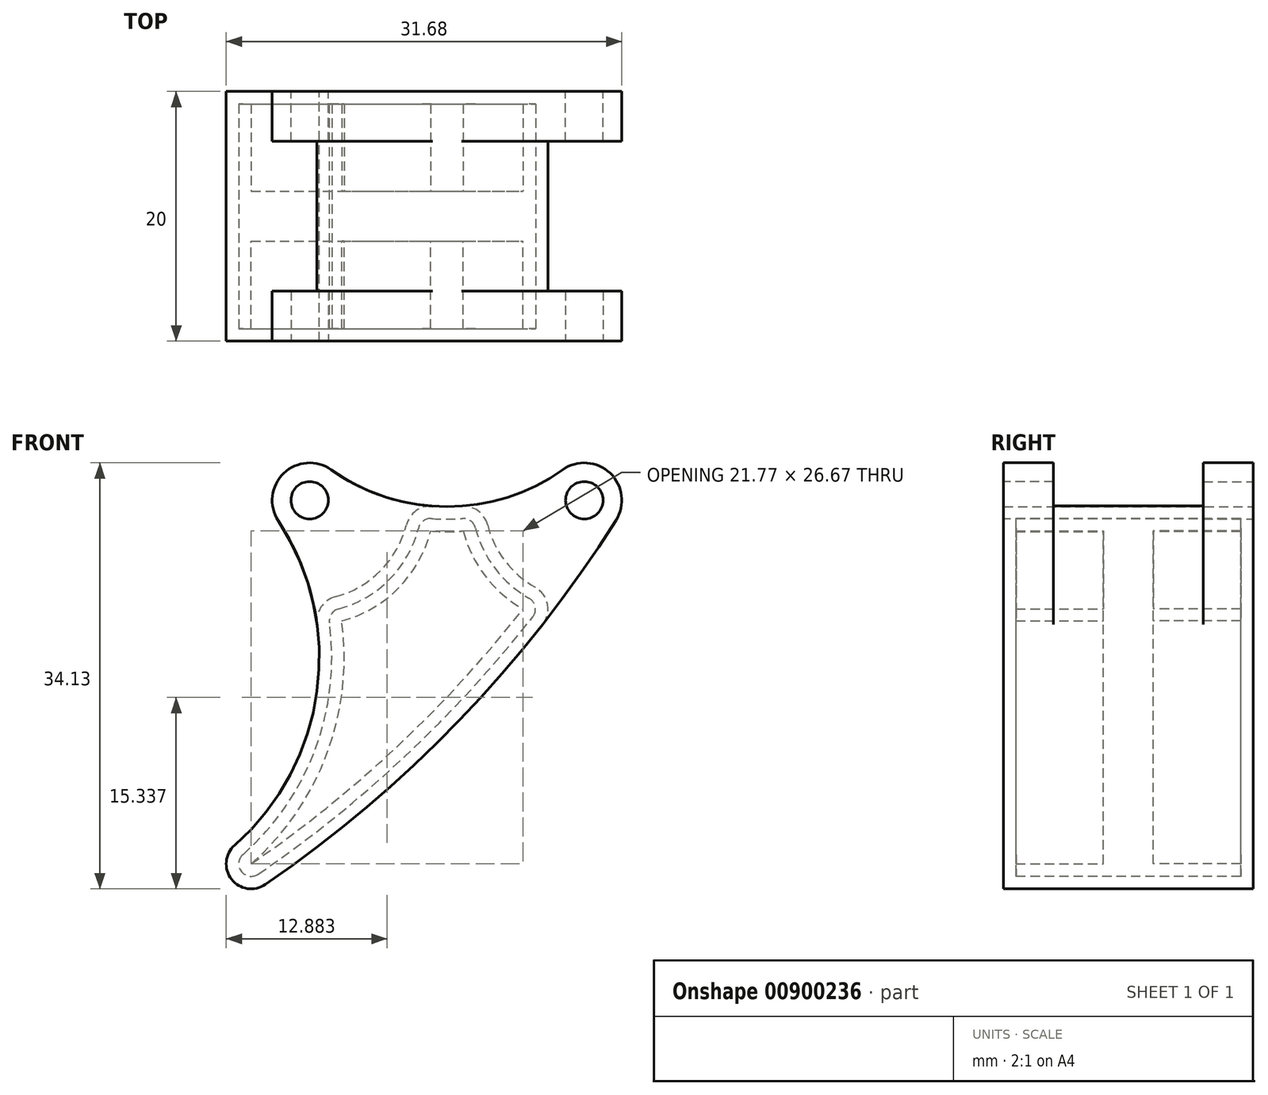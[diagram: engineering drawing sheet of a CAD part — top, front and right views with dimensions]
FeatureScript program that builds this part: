
annotation { "Feature Type Name" : "Feature", "Feature Type Description" : "" }
export const myFeature = defineFeature(function(context is Context, id is Id, definition is map)
    precondition{}
    {
        {
            var Q0;
            Q0=qCreatedBy(makeId("Front.planeOp"),FACE);
            var sketch = newSketch(context, id + "F0", { "sketchPlane" : qUnion([Q0])});
            skArc(sketch, "E0", {"start": v(1.74, 2.45) * mm, "mid": v(-2.08, 2.16) * mm, "end": v(-2.5, -1.65) * mm});
            skArc(sketch, "E1", {"start": v(24.54, -1.6) * mm, "mid": v(24.06, 2.18) * mm, "end": v(20.26, 2.45) * mm});
            skArc(sketch, "E2", {"start": v(1.74, 2.45) * mm, "mid": v(11, -0.5) * mm, "end": v(20.26, 2.45) * mm});
            skArc(sketch, "E3", {"start": v(-6, -27.63) * mm, "mid": v(0.6, -15.29) * mm, "end": v(-2.5, -1.65) * mm});
            skArc(sketch, "E4", {"start": v(-6, -27.63) * mm, "mid": v(-6.26, -30.35) * mm, "end": v(-3.55, -30.78) * mm});
            skArc(sketch, "E5", {"start": v(-3.55, -30.78) * mm, "mid": v(11.99, -17.62) * mm, "end": v(24.54, -1.6) * mm});
            skSolve(sketch);
        }
        {
            var Q0;
            Q0=makeQuery(id+"F0.imprint","IMPRINT",FACE,{"disambiguationData":[TD([[makeQuery(id+"F0.imprint","IMPRINT",EDGE,{"derivedFrom":sQuery(id+"F0.wireOp",EDGE,"E0")}),1.0]])]});
            extrude(context, id + "F1", {"entities" : qUnion([Q0]), "depth" : 4 * mm, "offsetDistance" : 25 * mm});
        }
        {
            var Q0;
            Q0=makeQuery(id+"F1.opExtrude","CAP_FACE",FACE,{"disambiguationData":[OSD([sQuery(id+"F0.wireOp",EDGE,"E0"),sQuery(id+"F0.wireOp",EDGE,"E1"),sQuery(id+"F0.wireOp",EDGE,"E2"),sQuery(id+"F0.wireOp",EDGE,"E3"),sQuery(id+"F0.wireOp",EDGE,"E4"),sQuery(id+"F0.wireOp",EDGE,"E5")])],"isStart":false});
            var sketch = newSketch(context, id + "F2", { "sketchPlane" : qUnion([Q0])});
            skArc(sketch, "E6", {"start": v(2.06, -7.73) * mm, "mid": v(5.69, -5.62) * mm, "end": v(7.75, -1.97) * mm});
            skArc(sketch, "E7", {"start": v(14.25, -1.97) * mm, "mid": v(15.65, -4.86) * mm, "end": v(18.07, -6.97) * mm});
            skArc(sketch, "E8.0", {"start": v(9.84, -0.47) * mm, "mid": v(11, -0.5) * mm, "end": v(12.16, -0.47) * mm});
            skArc(sketch, "E9.0", {"start": v(-6, -27.63) * mm, "mid": v(-0.49, -19.6) * mm, "end": v(0.6, -9.93) * mm});
            skArc(sketch, "E10.0", {"start": v(-6, -27.63) * mm, "mid": v(-6.26, -30.35) * mm, "end": v(-3.55, -30.78) * mm});
            skArc(sketch, "E11.0", {"start": v(-3.55, -30.78) * mm, "mid": v(8.35, -21.21) * mm, "end": v(18.66, -9.94) * mm});
            skPoint(sketch, "E12.newPointB", {"position": v(-2.5, -1.65) * mm});
            skArc(sketch, "E12.filletArc", {"start": v(2.06, -7.73) * mm, "mid": v(0.9, -8.55) * mm, "end": v(0.6, -9.93) * mm});
            skPoint(sketch, "E13.newPointB", {"position": v(1.74, 2.45) * mm});
            skArc(sketch, "E13.filletArc", {"start": v(9.84, -0.47) * mm, "mid": v(8.52, -0.84) * mm, "end": v(7.75, -1.97) * mm});
            skPoint(sketch, "E14.newPointA", {"position": v(20.26, 2.45) * mm});
            skArc(sketch, "E14.filletArc", {"start": v(14.25, -1.97) * mm, "mid": v(13.48, -0.84) * mm, "end": v(12.16, -0.47) * mm});
            skPoint(sketch, "E15.newPointB", {"position": v(24.54, -1.6) * mm});
            skArc(sketch, "E15.filletArc", {"start": v(18.66, -9.94) * mm, "mid": v(19.05, -8.32) * mm, "end": v(18.07, -6.97) * mm});
            skSolve(sketch);
        }
        {
            var Q0;
            Q0=makeQuery(id+"F2.imprint","IMPRINT",FACE,{"disambiguationData":[TD([[makeQuery(id+"F2.imprint","IMPRINT",EDGE,{"derivedFrom":sQuery(id+"F2.wireOp",EDGE,"E6")}),-1.0]])]});
            extrude(context, id + "F3", {"entities" : qUnion([Q0]), "operationType" : NewBodyOperationType.ADD, "depth" : 6 * mm, "offsetDistance" : 25 * mm});
        }
        {
            var Q0;
            Q0=makeQuery(id+"F3.opExtrude","CAP_FACE",FACE,{"disambiguationData":[OSD([sQuery(id+"F2.wireOp",EDGE,"E6"),sQuery(id+"F2.wireOp",EDGE,"E7"),sQuery(id+"F2.wireOp",EDGE,"E8.0"),sQuery(id+"F2.wireOp",EDGE,"E9.0"),sQuery(id+"F2.wireOp",EDGE,"E10.0"),sQuery(id+"F2.wireOp",EDGE,"E11.0"),sQuery(id+"F2.wireOp",EDGE,"E12.filletArc"),sQuery(id+"F2.wireOp",EDGE,"E13.filletArc"),sQuery(id+"F2.wireOp",EDGE,"E14.filletArc"),sQuery(id+"F2.wireOp",EDGE,"E15.filletArc")])],"isStart":false});
            var sketch = newSketch(context, id + "F4", { "sketchPlane" : qUnion([Q0])});
            skArc(sketch, "E16.0.0", {"start": v(-3.55, -30.78) * mm, "mid": v(8.35, -21.21) * mm, "end": v(18.66, -9.94) * mm});
            skArc(sketch, "E16.0.1", {"start": v(18.66, -9.94) * mm, "mid": v(19.05, -8.32) * mm, "end": v(18.07, -6.97) * mm});
            skArc(sketch, "E16.0.2", {"start": v(18.07, -6.97) * mm, "mid": v(15.65, -4.86) * mm, "end": v(14.25, -1.97) * mm});
            skArc(sketch, "E16.0.3", {"start": v(14.25, -1.97) * mm, "mid": v(13.48, -0.84) * mm, "end": v(12.16, -0.47) * mm});
            skArc(sketch, "E16.0.4", {"start": v(12.16, -0.47) * mm, "mid": v(11, -0.5) * mm, "end": v(9.84, -0.47) * mm});
            skArc(sketch, "E16.0.5", {"start": v(9.84, -0.47) * mm, "mid": v(8.52, -0.84) * mm, "end": v(7.75, -1.97) * mm});
            skArc(sketch, "E16.0.6", {"start": v(7.75, -1.97) * mm, "mid": v(5.69, -5.62) * mm, "end": v(2.06, -7.73) * mm});
            skArc(sketch, "E16.0.7", {"start": v(2.06, -7.73) * mm, "mid": v(0.9, -8.55) * mm, "end": v(0.6, -9.93) * mm});
            skArc(sketch, "E16.0.8", {"start": v(0.6, -9.93) * mm, "mid": v(-0.49, -19.6) * mm, "end": v(-6, -27.63) * mm});
            skArc(sketch, "E16.0.9", {"start": v(-6, -27.63) * mm, "mid": v(-6.26, -30.35) * mm, "end": v(-3.55, -30.78) * mm});
            skArc(sketch, "E17.0", {"start": v(-5.34, -28.38) * mm, "mid": v(-5.47, -29.74) * mm, "end": v(-4.12, -29.95) * mm});
            skArc(sketch, "E17.1", {"start": v(1.58, -9.8) * mm, "mid": v(0.45, -19.96) * mm, "end": v(-5.34, -28.38) * mm});
            skArc(sketch, "E17.2", {"start": v(-4.12, -29.95) * mm, "mid": v(7.67, -20.48) * mm, "end": v(17.87, -9.33) * mm});
            skArc(sketch, "E17.3", {"start": v(2.32, -8.7) * mm, "mid": v(1.74, -9.1) * mm, "end": v(1.58, -9.8) * mm});
            skArc(sketch, "E17.4", {"start": v(8.72, -2.21) * mm, "mid": v(6.4, -6.33) * mm, "end": v(2.32, -8.7) * mm});
            skArc(sketch, "E17.5", {"start": v(9.77, -1.46) * mm, "mid": v(9.1, -1.65) * mm, "end": v(8.72, -2.21) * mm});
            skArc(sketch, "E17.6", {"start": v(17.87, -9.33) * mm, "mid": v(18.07, -8.52) * mm, "end": v(17.58, -7.84) * mm});
            skArc(sketch, "E17.7", {"start": v(17.58, -7.84) * mm, "mid": v(14.85, -5.47) * mm, "end": v(13.28, -2.21) * mm});
            skArc(sketch, "E17.8", {"start": v(13.28, -2.21) * mm, "mid": v(12.9, -1.65) * mm, "end": v(12.23, -1.46) * mm});
            skArc(sketch, "E17.9", {"start": v(12.23, -1.46) * mm, "mid": v(11, -1.5) * mm, "end": v(9.77, -1.46) * mm});
            skSolve(sketch);
        }
        {
            var Q0;
            Q0=makeQuery(id+"F4.imprint","IMPRINT",FACE,{"disambiguationData":[TD([[makeQuery(id+"F4.imprint","IMPRINT",EDGE,{"derivedFrom":sQuery(id+"F4.wireOp",EDGE,"E17.0")}),1.0]])]});
            extrude(context, id + "F5", {"entities" : qUnion([Q0]), "operationType" : NewBodyOperationType.REMOVE, "oppositeDirection" : true, "depth" : 2 * mm, "offsetDistance" : 25 * mm});
        }
        {
            var Q0;
            Q0=makeQuery(id+"F5.boolean.opBoolean","COPY",FACE,{"derivedFrom":makeQuery(id+"F5.opExtrude","CAP_FACE",FACE,{"disambiguationData":[OSD([sQuery(id+"F4.wireOp",EDGE,"E17.0"),sQuery(id+"F4.wireOp",EDGE,"E17.1"),sQuery(id+"F4.wireOp",EDGE,"E17.2"),sQuery(id+"F4.wireOp",EDGE,"E17.3"),sQuery(id+"F4.wireOp",EDGE,"E17.4"),sQuery(id+"F4.wireOp",EDGE,"E17.5"),sQuery(id+"F4.wireOp",EDGE,"E17.6"),sQuery(id+"F4.wireOp",EDGE,"E17.7"),sQuery(id+"F4.wireOp",EDGE,"E17.8"),sQuery(id+"F4.wireOp",EDGE,"E17.9")])],"isStart":false})});
            var sketch = newSketch(context, id + "F6", { "sketchPlane" : qUnion([Q0])});
            skArc(sketch, "E18.0.0", {"start": v(13.28, -2.21) * mm, "mid": v(12.9, -1.65) * mm, "end": v(12.23, -1.46) * mm});
            skArc(sketch, "E18.0.1", {"start": v(12.23, -1.46) * mm, "mid": v(11, -1.5) * mm, "end": v(9.77, -1.46) * mm});
            skArc(sketch, "E18.0.2", {"start": v(9.77, -1.46) * mm, "mid": v(9.1, -1.65) * mm, "end": v(8.72, -2.21) * mm});
            skArc(sketch, "E18.0.3", {"start": v(8.72, -2.21) * mm, "mid": v(6.4, -6.33) * mm, "end": v(2.32, -8.7) * mm});
            skArc(sketch, "E18.0.4", {"start": v(2.32, -8.7) * mm, "mid": v(1.74, -9.1) * mm, "end": v(1.58, -9.8) * mm});
            skArc(sketch, "E18.0.5", {"start": v(1.58, -9.8) * mm, "mid": v(0.45, -19.96) * mm, "end": v(-5.34, -28.38) * mm});
            skArc(sketch, "E18.0.6", {"start": v(-5.34, -28.38) * mm, "mid": v(-5.47, -29.74) * mm, "end": v(-4.12, -29.95) * mm});
            skArc(sketch, "E18.0.7", {"start": v(-4.12, -29.95) * mm, "mid": v(7.67, -20.48) * mm, "end": v(17.87, -9.33) * mm});
            skArc(sketch, "E18.0.8", {"start": v(17.87, -9.33) * mm, "mid": v(18.07, -8.52) * mm, "end": v(17.58, -7.84) * mm});
            skArc(sketch, "E18.0.9", {"start": v(17.58, -7.84) * mm, "mid": v(14.85, -5.47) * mm, "end": v(13.28, -2.21) * mm});
            skArc(sketch, "E19.0", {"start": v(17.09, -8.71) * mm, "mid": v(14.06, -6.08) * mm, "end": v(12.3, -2.46) * mm});
            skLineSegment(sketch, "E19.1", {"start": v(17.09, -8.71) * mm, "end": v(17.09, -8.71) * mm});
            skLineSegment(sketch, "E19.2", {"start": v(12.3, -2.46) * mm, "end": v(12.3, -2.46) * mm});
            skArc(sketch, "E19.3", {"start": v(-4.68, -29.13) * mm, "mid": v(6.98, -19.75) * mm, "end": v(17.09, -8.71) * mm});
            skLineSegment(sketch, "E19.4", {"start": v(-4.68, -29.13) * mm, "end": v(-4.68, -29.13) * mm});
            skArc(sketch, "E19.5", {"start": v(2.57, -9.66) * mm, "mid": v(1.39, -20.3) * mm, "end": v(-4.68, -29.13) * mm});
            skArc(sketch, "E19.6", {"start": v(12.3, -2.46) * mm, "mid": v(11, -2.5) * mm, "end": v(9.7, -2.46) * mm});
            skLineSegment(sketch, "E19.7", {"start": v(9.7, -2.46) * mm, "end": v(9.7, -2.46) * mm});
            skArc(sketch, "E19.8", {"start": v(9.7, -2.46) * mm, "mid": v(7.11, -7.03) * mm, "end": v(2.57, -9.66) * mm});
            skLineSegment(sketch, "E19.9", {"start": v(2.57, -9.66) * mm, "end": v(2.57, -9.66) * mm});
            skSolve(sketch);
        }
        {
            var Q0;
            Q0=makeQuery(id+"F6.imprint","IMPRINT",FACE,{"disambiguationData":[TD([[makeQuery(id+"F6.imprint","IMPRINT",EDGE,{"derivedFrom":sQuery(id+"F6.wireOp",EDGE,"E19.0")}),1.0]])]});
            extrude(context, id + "F7", {"entities" : qUnion([Q0]), "operationType" : NewBodyOperationType.REMOVE, "oppositeDirection" : true, "depth" : 7 * mm, "offsetDistance" : 25 * mm});
        }
        {
            var Q0;
            Q0=qCreatedBy(makeId("Front.planeOp"),FACE);
            var sketch = newSketch(context, id + "F8", { "sketchPlane" : qUnion([Q0])});
            skCircle(sketch, "E20", {"center": v(0, 0) * mm, "radius": 1.5 * mm});
            skCircle(sketch, "E21", {"center": v(22, 0) * mm, "radius": 1.5 * mm});
            skSolve(sketch);
        }
        {
            var Q0;
            Q0 = qSketchRegion(id + "F8", true);
            extrude(context, id + "F9", {"entities" : qUnion([Q0]), "operationType" : NewBodyOperationType.REMOVE, "endBound" : BoundingType.THROUGH_ALL, "depth" : 25 * mm, "offsetDistance" : 25 * mm});
        }
        {
            var Q0;
            Q0=makeQuery(id+"F1.opExtrude","SWEPT_BODY",BODY,{"disambiguationData":[OSD([sQuery(id+"F0.wireOp",EDGE,"E0"),sQuery(id+"F0.wireOp",EDGE,"E1"),sQuery(id+"F0.wireOp",EDGE,"E2"),sQuery(id+"F0.wireOp",EDGE,"E3"),sQuery(id+"F0.wireOp",EDGE,"E4"),sQuery(id+"F0.wireOp",EDGE,"E5")])]});
            var Q1;
            Q1=makeQuery(id+"F3.opExtrude","CAP_FACE",FACE,{"disambiguationData":[OSD([sQuery(id+"F2.wireOp",EDGE,"E6"),sQuery(id+"F2.wireOp",EDGE,"E7"),sQuery(id+"F2.wireOp",EDGE,"E8.0"),sQuery(id+"F2.wireOp",EDGE,"E9.0"),sQuery(id+"F2.wireOp",EDGE,"E10.0"),sQuery(id+"F2.wireOp",EDGE,"E11.0"),sQuery(id+"F2.wireOp",EDGE,"E12.filletArc"),sQuery(id+"F2.wireOp",EDGE,"E13.filletArc"),sQuery(id+"F2.wireOp",EDGE,"E14.filletArc"),sQuery(id+"F2.wireOp",EDGE,"E15.filletArc")])],"isStart":false});
            mirror(context, id + "F10", {"operationType" : NewBodyOperationType.ADD, "entities" : qUnion([Q0]), "mirrorPlane" : qUnion([Q1])});
        }
    });
